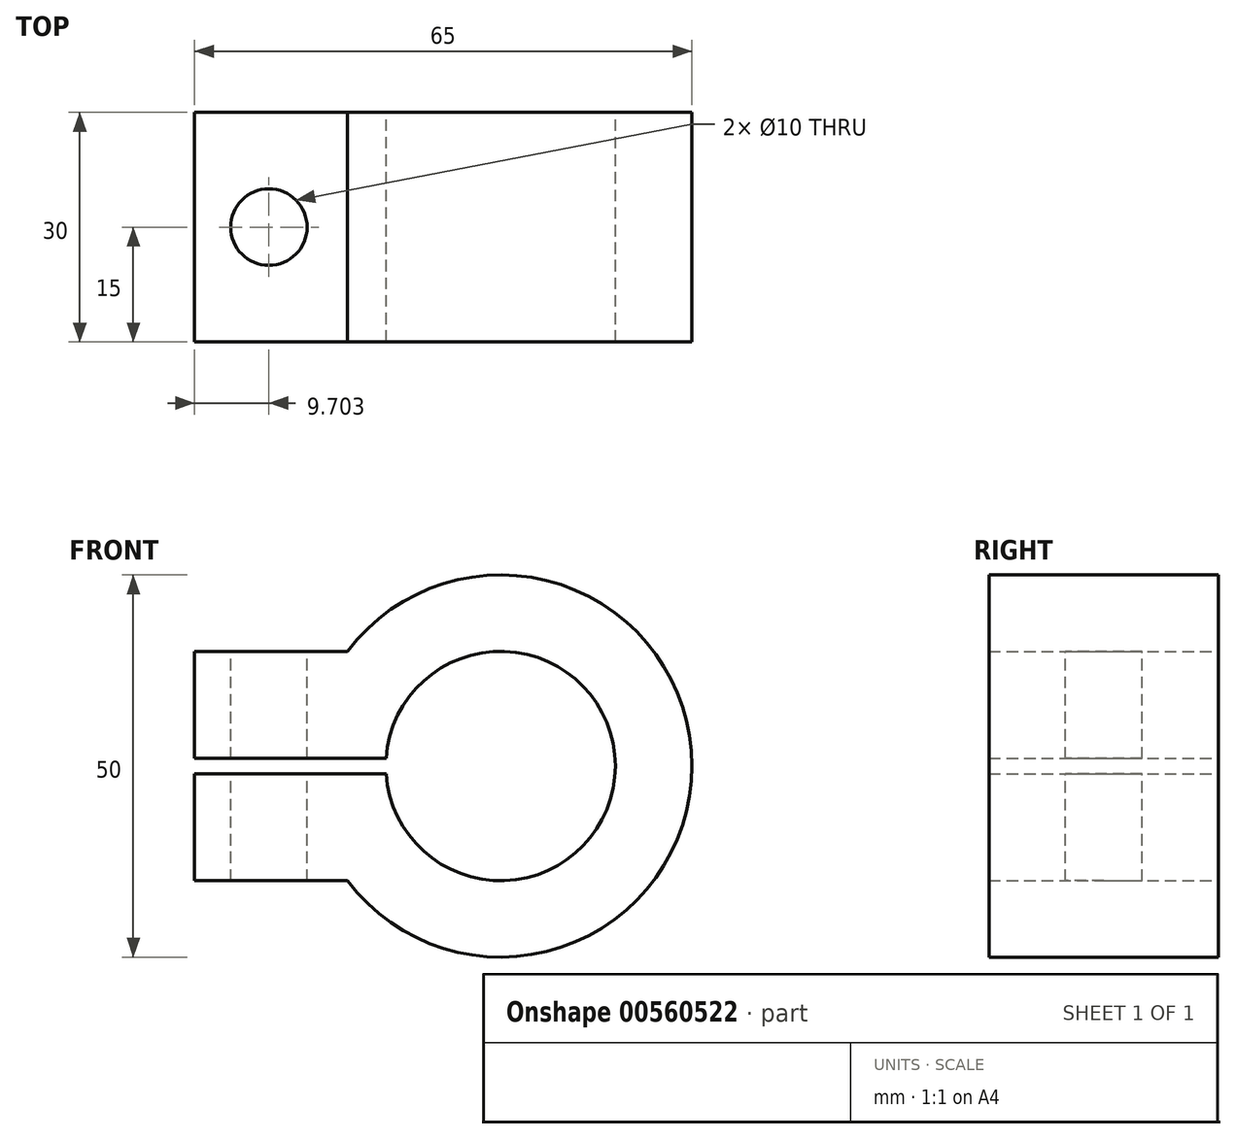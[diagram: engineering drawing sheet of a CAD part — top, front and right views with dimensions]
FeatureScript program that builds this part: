
annotation { "Feature Type Name" : "Feature", "Feature Type Description" : "" }
export const myFeature = defineFeature(function(context is Context, id is Id, definition is map)
    precondition{}
    {
        {
            var Q0;
            Q0=qCreatedBy(makeId("Front.planeOp"),FACE);
            var sketch = newSketch(context, id + "F0", { "sketchPlane" : qUnion([Q0])});
            skCircle(sketch, "E0", {"center": v(0, 0) * mm, "radius": 15 * mm});
            skCircle(sketch, "E1", {"center": v(0, 0) * mm, "radius": 25 * mm});
            skLineSegment(sketch, "E2", {"start": v(-20, 15) * mm, "end": v(-40, 15) * mm});
            skLineSegment(sketch, "E3", {"start": v(-20, -15) * mm, "end": v(-40, -15) * mm});
            skLineSegment(sketch, "E4", {"start": v(-40, 15) * mm, "end": v(-40, 1) * mm});
            skLineSegment(sketch, "E5", {"start": v(-40, 1) * mm, "end": v(-14.97, 1) * mm});
            skLineSegment(sketch, "E6", {"start": v(-40, -15) * mm, "end": v(-40, -1) * mm});
            skLineSegment(sketch, "E7", {"start": v(-40, -1) * mm, "end": v(-14.97, -1) * mm});
            skSolve(sketch);
        }
        {
            var Q0;
            {var subQ0=sQuery(id+"F0.wireOp",EDGE,"E2");Q0=makeQuery(id+"F0.imprint","IMPRINT",FACE,{"disambiguationData":[TD([[makeQuery(id+"F0.imprint","IMPRINT",EDGE,{"derivedFrom":subQ0}),1.0]])]});}
            var Q1;
            {var subQ5=sQuery(id+"F0.wireOp",EDGE,"E5");var subQ7=sQuery(id+"F0.wireOp",EDGE,"E0");var subQ9=makeQuery(id+"F0.imprint","INTERSECT",VERTEX,{"derivedFrom":[subQ7,subQ5]});Q1=makeQuery(id+"F0.imprint","IMPRINT",FACE,{"disambiguationData":[TD([[makeQuery(id+"F0.imprint","IMPRINT",EDGE,{"disambiguationData":[TD([[subQ9,1.0]])],"derivedFrom":subQ7}),-1.0]])]});}
            var Q2;
            {var subQ0=sQuery(id+"F0.wireOp",EDGE,"E3");Q2=makeQuery(id+"F0.imprint","IMPRINT",FACE,{"disambiguationData":[TD([[makeQuery(id+"F0.imprint","IMPRINT",EDGE,{"derivedFrom":subQ0}),-1.0]])]});}
            extrude(context, id + "F1", {"entities" : qUnion([Q0, Q1, Q2]), "depth" : 30 * mm, "offsetDistance" : 25 * mm});
        }
        {
            var Q0;
            Q0=makeQuery(id+"F1.opExtrude","SWEPT_FACE",FACE,{"disambiguationData":[OSD([sQuery(id+"F0.wireOp",EDGE,"E2")])]});
            var sketch = newSketch(context, id + "F2", { "sketchPlane" : qUnion([Q0])});
            skCircle(sketch, "E8", {"center": v(-30.3, -15) * mm, "radius": 5 * mm});
            skPoint(sketch, "E8.centerSnap0", {"position": v(-40, -15) * mm});
            skSolve(sketch);
        }
        {
            var Q0;
            Q0=makeQuery(id+"F2.imprint","IMPRINT",FACE,{"disambiguationData":[TD([[makeQuery(id+"F2.imprint","IMPRINT",EDGE,{"derivedFrom":sQuery(id+"F2.wireOp",EDGE,"E8")}),1.0]])]});
            extrude(context, id + "F3", {"entities" : qUnion([Q0]), "operationType" : NewBodyOperationType.REMOVE, "endBound" : BoundingType.THROUGH_ALL, "oppositeDirection" : true, "depth" : 25 * mm, "offsetDistance" : 25 * mm});
        }
    });
